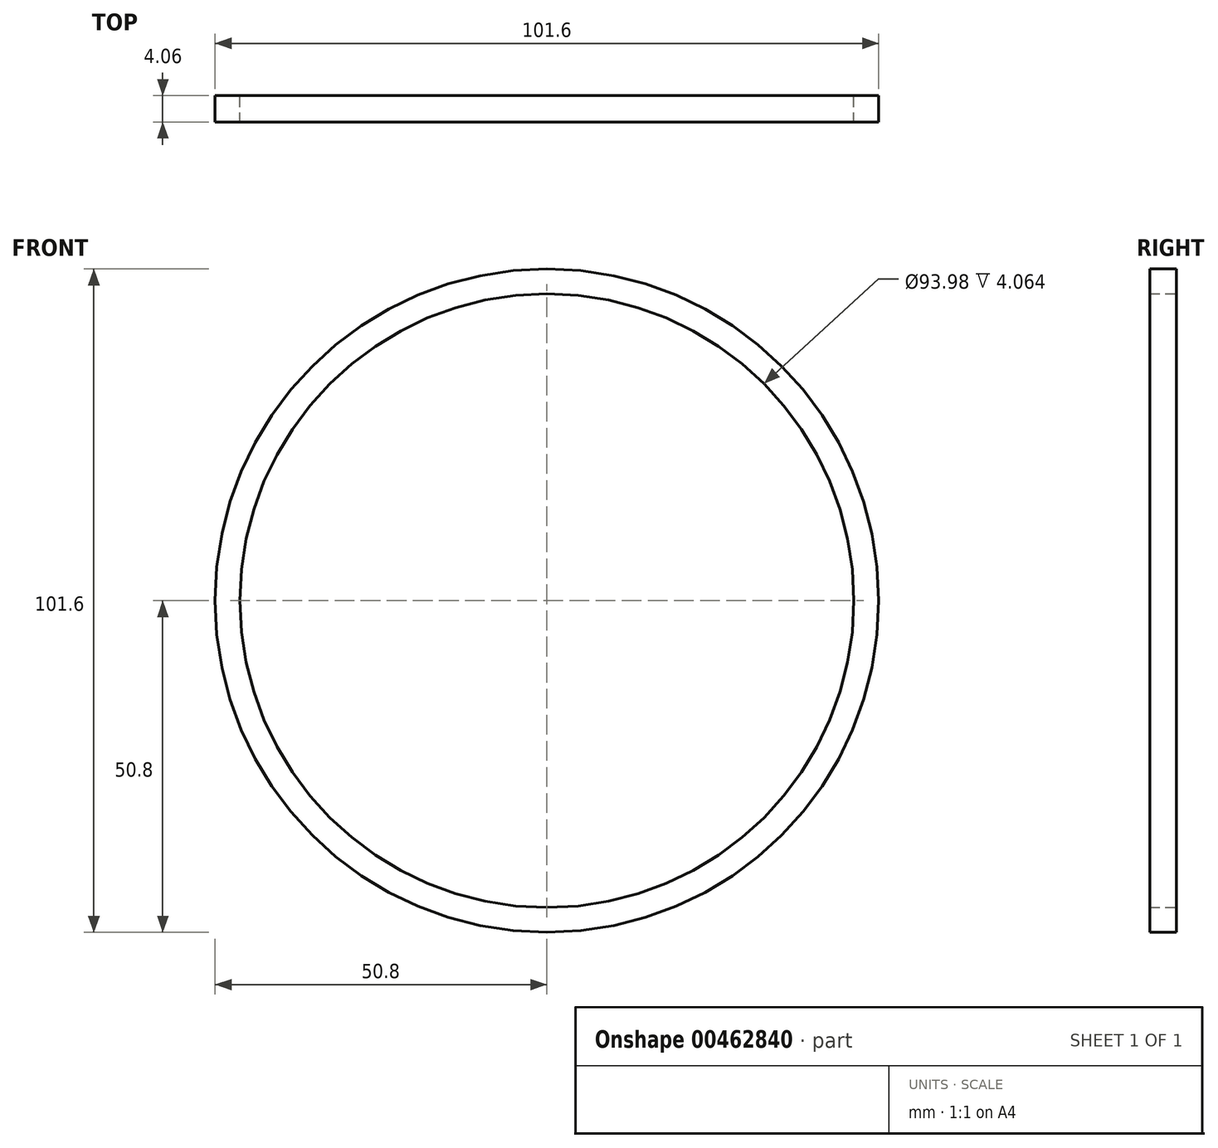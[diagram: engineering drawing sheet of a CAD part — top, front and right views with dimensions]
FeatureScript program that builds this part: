
annotation { "Feature Type Name" : "Feature", "Feature Type Description" : "" }
export const myFeature = defineFeature(function(context is Context, id is Id, definition is map)
    precondition{}
    {
        {
            var Q0;
            Q0=qCreatedBy(makeId("Front.planeOp"),FACE);
            var sketch = newSketch(context, id + "F0", { "sketchPlane" : qUnion([Q0])});
            skCircle(sketch, "E0", {"center": v(0, 0) * mm, "radius": 50.8 * mm});
            skCircle(sketch, "E1", {"center": v(0, 0) * mm, "radius": 47 * mm});
            skSolve(sketch);
        }
        {
            var Q0;
            Q0=makeQuery(id+"F0.imprint","IMPRINT",FACE,{"disambiguationData":[TD([[makeQuery(id+"F0.imprint","IMPRINT",EDGE,{"derivedFrom":sQuery(id+"F0.wireOp",EDGE,"E0")}),1.0]])]});
            extrude(context, id + "F1", {"entities" : qUnion([Q0]), "depth" : 4.06 * mm});
        }
    });
